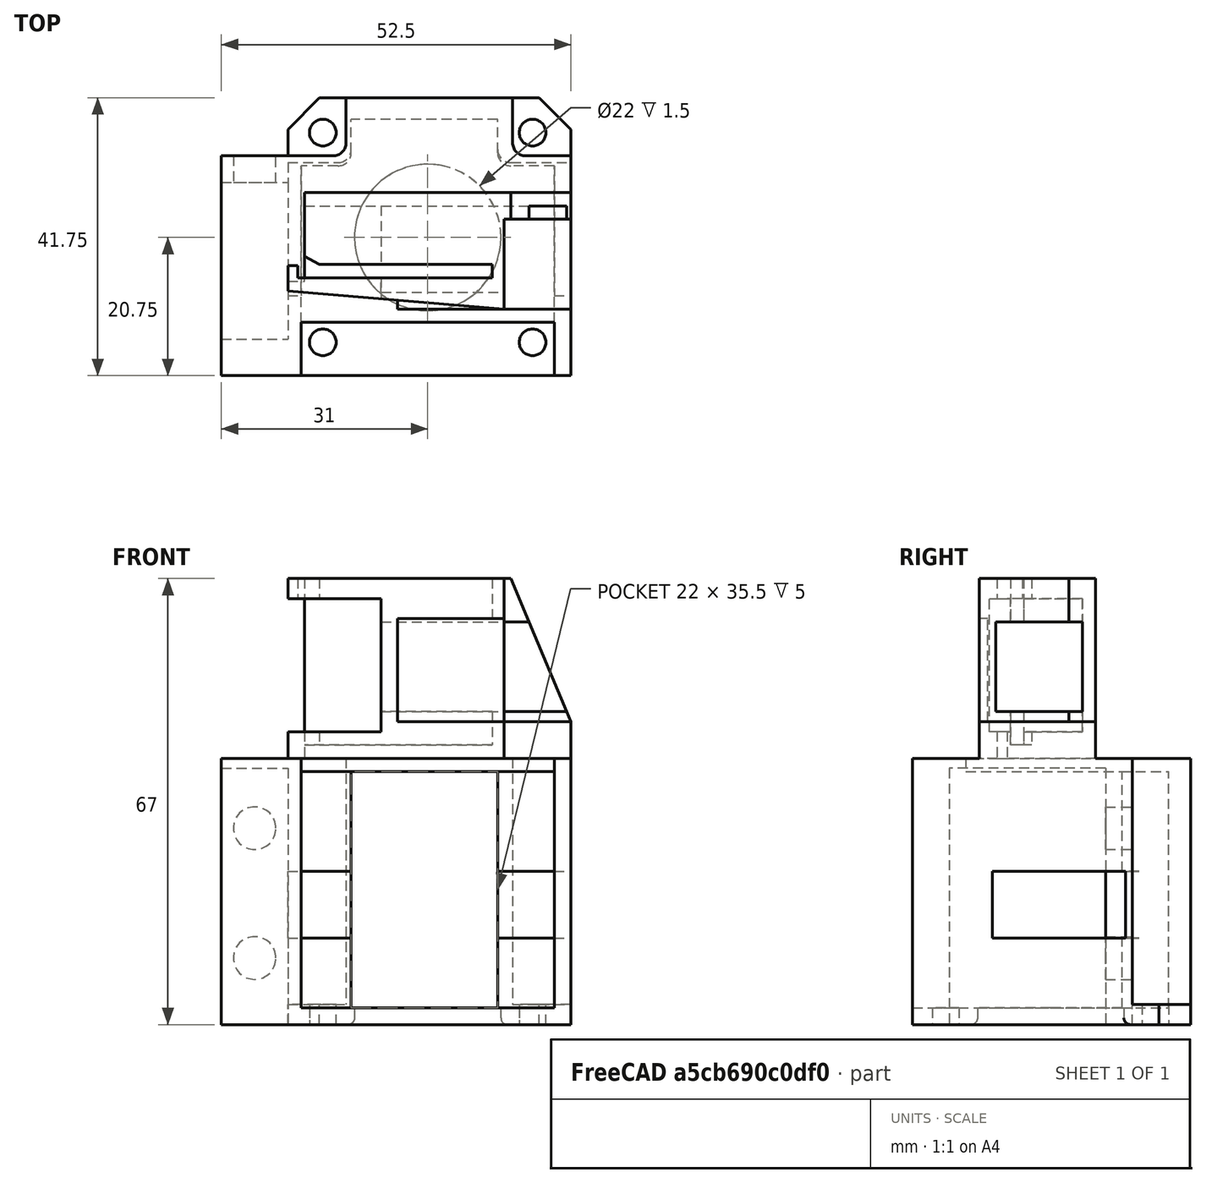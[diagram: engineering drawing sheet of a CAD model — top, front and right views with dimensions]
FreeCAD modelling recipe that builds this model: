
FCSTD DOCUMENT  (FreeCAD 0.20R29410 (Git))
Label: drive_holder
License: All rights reserved
LicenseURL: http://en.wikipedia.org/wiki/All_rights_reserved
objects: Sketcher::SketchObject×20, PartDesign::Pocket×17, PartDesign::Pad×3, PartDesign::Fillet×3, PartDesign::Body×2, Part::Fuse×1, Mesh::Feature×1
note: 69 computed .brp shape members not serialized (recipe doc carries the construction recipe); baked Part::Feature solids carry a one-line shape summary decoded from their .brp

FEATURE [Sketcher::SketchObject] Sketch
  FullyConstrained = true
  MapMode = 5
  Support = -> [XY_Plane]
  sketch-geometry (8):
    g0: LineSegment StartX=0 StartY=0 StartZ=0 EndX=-52.5 EndY=0 EndZ=0
    g1: LineSegment StartX=-52.5 StartY=0 StartZ=0 EndX=-52.5 EndY=33 EndZ=0
    g2: LineSegment StartX=-52.5 StartY=33 StartZ=0 EndX=-42.5 EndY=33 EndZ=0
    g3: LineSegment StartX=-42.5 StartY=33 StartZ=0 EndX=-42.5 EndY=37 EndZ=0
    g4: LineSegment StartX=-42.5 StartY=37 StartZ=0 EndX=-37.75 EndY=41.75 EndZ=0
    g5: LineSegment StartX=-37.75 StartY=41.75 StartZ=0 EndX=-4.75 EndY=41.75 EndZ=0
    g6: LineSegment StartX=-4.75 StartY=41.75 StartZ=0 EndX=0 EndY=37 EndZ=0
    g7: LineSegment StartX=0 StartY=37 StartZ=0 EndX=0 EndY=0 EndZ=0
  constraints (23):
    c: Coincident(g0,g-1)
    c: PointOnObject(g0,g-1)
    c: Coincident(g1,g0)
    c: Vertical(g1)
    c: Coincident(g2,g1)
    c: Horizontal(g2)
    c: Coincident(g3,g2)
    c: Vertical(g3)
    c: Coincident(g4,g3)
    c: Coincident(g5,g4)
    c: Horizontal(g5)
    c: Coincident(g6,g5)
    c: PointOnObject(g6,g-2)
    c: Coincident(g7,g6)
    c: Coincident(g7,g0)
    c: DistanceX(g5,g5) = 33
    c: DistanceX(g0,g0) = 52.5
    c: DistanceX(g2,g2) = 10
    c: Horizontal(g3,g6)
    c: Angle(g5,g6) = 2.35619
    c: Angle(g4,g5) = 2.35619
    c: DistanceY(g0,g6) = 37
    c: DistanceY(g1,g1) = 33
FEATURE [PartDesign::Pad] Pad  label="to_drive_bodie"
  Direction = (0,0,1)
  Length = 40
  Length2 = 10
  Profile = -> Sketch
  ReferenceAxis = -> Sketch [N_Axis]
  Type = 0
FEATURE [Sketcher::SketchObject] Sketch001
  ExternalGeometry = -> [Pad]
  FullyConstrained = true
  MapMode = 5
  Placement = pos=(0,0,40) rot=(0,0,1;0rad)
  Support = -> [Pad]
  sketch-geometry (10):
    g0: LineSegment StartX=-42.5 StartY=33 StartZ=0 EndX=-42.5 EndY=37 EndZ=0
    g1: LineSegment StartX=-42.5 StartY=37 StartZ=0 EndX=-37.75 EndY=41.75 EndZ=0
    g2: LineSegment StartX=-37.75 StartY=41.75 StartZ=0 EndX=-33.75 EndY=41.75 EndZ=0
    g3: LineSegment StartX=-33.75 StartY=41.75 StartZ=0 EndX=-33.75 EndY=33 EndZ=0
    g4: LineSegment StartX=-33.75 StartY=33 StartZ=0 EndX=-42.5 EndY=33 EndZ=0
    g5: LineSegment StartX=-8.75 StartY=41.75 StartZ=0 EndX=-4.75 EndY=41.75 EndZ=0
    g6: LineSegment StartX=-4.75 StartY=41.75 StartZ=0 EndX=0 EndY=37 EndZ=0
    g7: LineSegment StartX=0 StartY=37 StartZ=0 EndX=0 EndY=33 EndZ=0
    g8: LineSegment StartX=0 StartY=33 StartZ=0 EndX=-8.75 EndY=33 EndZ=0
    g9: LineSegment StartX=-8.75 StartY=33 StartZ=0 EndX=-8.75 EndY=41.75 EndZ=0
  constraints (26):
    c: Coincident(g1,g0)
    c: Coincident(g2,g1)
    c: Coincident(g3,g2)
    c: Vertical(g3)
    c: Coincident(g4,g3)
    c: Coincident(g4,g0)
    c: Horizontal(g4)
    c: Coincident(g6,g5)
    c: Coincident(g7,g6)
    c: Coincident(g8,g7)
    c: Horizontal(g8)
    c: Coincident(g9,g8)
    c: Coincident(g9,g5)
    c: Vertical(g9)
    c: Vertical(g7)
    c: Horizontal(g2)
    c: Horizontal(g5)
    c: Coincident(g5,g-3)
    c: Coincident(g6,g-3)
    c: Coincident(g-4,g1)
    c: Coincident(g0,g-4)
    c: Equal(g0,g2)
    c: Equal(g2,g5)
    c: Equal(g5,g7)
    c: Coincident(g0,g-5)
    c: DistanceX(g2,g2) = 4
FEATURE [PartDesign::Pocket] Pocket  label="to_drive_screw_handler"
  BaseFeature = -> Pad
  Direction = (0,0,-1)
  Length = 37
  Length2 = 5
  Profile = -> Sketch001
  ReferenceAxis = -> Sketch001 [N_Axis]
  Type = 0
FEATURE [Sketcher::SketchObject] Sketch002
  ExternalGeometry = -> [Pocket]
  FullyConstrained = true
  MapMode = 5
  Placement = pos=(0,0,0) rot=(1,0,0;3.14159rad)
  Support = -> [Pocket]
  sketch-geometry (2):
    g0: Circle CenterX=-37.25 CenterY=-36.5 CenterZ=0 NormalX=0 NormalY=0 NormalZ=1 AngleXU=0 Radius=2
    g1: Circle CenterX=-5.75 CenterY=-36.5 CenterZ=0 NormalX=0 NormalY=0 NormalZ=1 AngleXU=0 Radius=2
  constraints (6):
    c: DistanceX(g0,g1) = 31.5
    c: Equal(g0,g1)
    c: Diameter(g0) = 4
    c: Horizontal(g1,g0)
    c: DistanceX(g-4,g0) = 0.5
    c: DistanceY(g-3,g0) = 0.5
FEATURE [PartDesign::Pocket] Pocket001  label="to_drive_screw_hole_upper"
  BaseFeature = -> Pocket
  Direction = (0,0,1)
  Length = 3
  Length2 = 5
  Profile = -> Sketch002
  ReferenceAxis = -> Sketch002 [N_Axis]
  Type = 0
FEATURE [Sketcher::SketchObject] Sketch003
  ExternalGeometry = -> [Pocket001]
  FullyConstrained = true
  MapMode = 5
  Placement = pos=(0,0,0) rot=(1,0,0;3.14159rad)
  Support = -> [Pocket001]
  sketch-geometry (2):
    g0: Circle CenterX=-37.25 CenterY=-5 CenterZ=0 NormalX=0 NormalY=0 NormalZ=1 AngleXU=0 Radius=2
    g1: Circle CenterX=-5.75 CenterY=-5 CenterZ=0 NormalX=0 NormalY=0 NormalZ=1 AngleXU=0 Radius=2
  constraints (6):
    c: Equal(g1,g0)
    c: Vertical(g1,g-4)
    c: Vertical(g0,g-3)
    c: Horizontal(g0,g1)
    c: Equal(g1,g-4)
    c: DistanceY(g-3,g0) = 31.5
FEATURE [PartDesign::Pocket] Pocket002  label="to_drive_screw_hole_lower"
  BaseFeature = -> Pocket001
  Direction = (0,0,1)
  Length = 3
  Length2 = 5
  Profile = -> Sketch003
  ReferenceAxis = -> Sketch003 [N_Axis]
  Type = 0
FEATURE [Sketcher::SketchObject] Sketch004
  ExternalGeometry = -> [Pocket002]
  FullyConstrained = true
  MapMode = 5
  Placement = pos=(0,0,0) rot=(1,0,0;3.14159rad)
  Support = -> [Pocket002]
  sketch-geometry (3):
    g0: LineSegment StartX=-37.25 StartY=-5 StartZ=0 EndX=-5.75 EndY=-36.5 EndZ=0
    g1: LineSegment StartX=-5.75 StartY=-5 StartZ=0 EndX=-37.25 EndY=-36.5 EndZ=0
    g2: Circle CenterX=-21.5 CenterY=-20.75 CenterZ=0 NormalX=0 NormalY=0 NormalZ=1 AngleXU=0 Radius=11
  constraints (7):
    c: Coincident(g0,g-3)
    c: Coincident(g0,g-5)
    c: Coincident(g1,g-4)
    c: Coincident(g1,g-6)
    c: PointOnObject(g2,g0)
    c: PointOnObject(g2,g1)
    c: Diameter(g2) = 22
FEATURE [PartDesign::Pocket] Pocket003  label="to_drive_hole"
  BaseFeature = -> Pocket002
  Direction = (0,0,1)
  Length = 5
  Length2 = 5
  Profile = -> Sketch004
  ReferenceAxis = -> Sketch004 [N_Axis]
  Type = 0
FEATURE [Sketcher::SketchObject] Sketch005
  ExternalGeometry = -> [Pocket003]
  FullyConstrained = true
  MapMode = 5
  Placement = pos=(-52.5,0,0) rot=(0.57735,-0.57735,-0.57735;2.0944rad)
  Support = -> [Pocket003]
  sketch-geometry (4):
    g0: LineSegment StartX=-29 StartY=38.5 StartZ=0 EndX=-5.5 EndY=38.5 EndZ=0
    g1: LineSegment StartX=-5.5 StartY=38.5 StartZ=0 EndX=-5.5 EndY=0 EndZ=0
    g2: LineSegment StartX=-29 StartY=0 StartZ=0 EndX=-5.5 EndY=0 EndZ=0
    g3: LineSegment StartX=-29 StartY=38.5 StartZ=0 EndX=-29 EndY=0 EndZ=0
  constraints (12):
    c: DistanceX(g-3,g2) = 4
    c: DistanceY(g0,g-5) = 1.5
    c: Horizontal(g0)
    c: DistanceX(g0,g-5) = 5.5
    c: Coincident(g1,g0)
    c: Vertical(g1)
    c: PointOnObject(g1,g-3)
    c: Coincident(g2,g1)
    c: Coincident(g3,g0)
    c: Vertical(g3)
    c: Coincident(g2,g3)
    c: PointOnObject(g2,g-3)
FEATURE [PartDesign::Pocket] Pocket004  label="to_guide_holder"
  BaseFeature = -> Pocket003
  Direction = (1,0,0)
  Length = 10
  Length2 = 5
  Profile = -> Sketch005
  ReferenceAxis = -> Sketch005 [N_Axis]
  Type = 0
FEATURE [Sketcher::SketchObject] Sketch006
  FullyConstrained = true
  MapMode = 5
  Placement = pos=(-42.5,0,0) rot=(0.57735,-0.57735,-0.57735;2.0944rad)
  Support = -> [Pocket004]
  sketch-geometry (8):
    g0: LineSegment StartX=0 StartY=0 StartZ=0 EndX=-32 EndY=0 EndZ=0
    g1: LineSegment StartX=-32 StartY=0 StartZ=0 EndX=-32 EndY=13 EndZ=0
    g2: LineSegment StartX=-32 StartY=13 StartZ=0 EndX=0 EndY=13 EndZ=0
    g3: LineSegment StartX=0 StartY=13 StartZ=0 EndX=0 EndY=0 EndZ=0
    g4: LineSegment StartX=-32 StartY=13 StartZ=0 EndX=-12 EndY=13 EndZ=0
    g5: LineSegment StartX=-12 StartY=13 StartZ=0 EndX=-12 EndY=23 EndZ=0
    g6: LineSegment StartX=-12 StartY=23 StartZ=0 EndX=-32 EndY=23 EndZ=0
    g7: LineSegment StartX=-32 StartY=23 StartZ=0 EndX=-32 EndY=13 EndZ=0
  constraints (22):
    c: Coincident(g0,g1)
    c: Coincident(g1,g2)
    c: Coincident(g2,g3)
    c: Coincident(g3,g0)
    c: Horizontal(g0)
    c: Horizontal(g2)
    c: Vertical(g1)
    c: Vertical(g3)
    c: Coincident(g0,g-1)
    c: Coincident(g4,g5)
    c: Coincident(g5,g6)
    c: Coincident(g6,g7)
    c: Coincident(g7,g4)
    c: Horizontal(g4)
    c: Horizontal(g6)
    c: Vertical(g5)
    c: Vertical(g7)
    c: Coincident(g4,g1)
    c: DistanceY(g3,g3) = 13
    c: DistanceX(g0,g0) = 32
    c: DistanceY(g5,g5) = 10
    c: DistanceX(g6,g6) = 20
FEATURE [PartDesign::Pocket] Pocket005  label="belt_hole"
  BaseFeature = -> Pocket004
  Direction = (1,0,0)
  Length = 5
  Length2 = 5
  Profile = -> Sketch006
  ReferenceAxis = -> Sketch006 [N_Axis]
  Type = 1
FEATURE [Sketcher::SketchObject] Sketch007
  FullyConstrained = true
  MapMode = 5
  Placement = pos=(0,33,0) rot=(0,0.707107,0.707107;3.14159rad)
  Support = -> [Pocket005]
  sketch-geometry (6):
    g0: Circle CenterX=47.5 CenterY=29.5 CenterZ=0 NormalX=0 NormalY=0 NormalZ=1 AngleXU=0 Radius=3.2
    g1: Circle CenterX=47.5 CenterY=10 CenterZ=0 NormalX=0 NormalY=0 NormalZ=1 AngleXU=0 Radius=3.2
    g2: LineSegment StartX=0 StartY=0 StartZ=0 EndX=47.5 EndY=0 EndZ=0
    g3: LineSegment StartX=47.5 StartY=0 StartZ=0 EndX=47.5 EndY=10 EndZ=0
    g4: LineSegment StartX=47.5 StartY=10 StartZ=0 EndX=0 EndY=10 EndZ=0
    g5: LineSegment StartX=0 StartY=10 StartZ=0 EndX=0 EndY=0 EndZ=0
  constraints (16):
    c: Equal(g0,g1)
    c: Radius(g0) = 3.2
    c: Coincident(g2,g3)
    c: Coincident(g3,g4)
    c: Coincident(g4,g5)
    c: Coincident(g5,g2)
    c: Horizontal(g2)
    c: Horizontal(g4)
    c: Vertical(g3)
    c: Vertical(g5)
    c: Coincident(g3,g1)
    c: DistanceY(g3,g3) = 10
    c: DistanceY(g1,g0) = 19.5
    c: Coincident(g-1,g2)
    c: Vertical(g1,g0)
    c: DistanceX(g2,g2) = 47.5
FEATURE [PartDesign::Pocket] Pocket006  label="to_guide_screw_hole"
  BaseFeature = -> Pocket005
  Direction = (0,-1,2e-16)
  Length = 4
  Length2 = 5
  Profile = -> Sketch007
  ReferenceAxis = -> Sketch007 [N_Axis]
  Type = 0
FEATURE [Sketcher::SketchObject] Sketch008
  FullyConstrained = true
  MapMode = 5
  Placement = pos=(0,0,40) rot=(0,0,1;0rad)
  Support = -> [Pocket006]
  sketch-geometry (4):
    g0: LineSegment StartX=-2.5 StartY=0 StartZ=0 EndX=-40.5 EndY=0 EndZ=0
    g1: LineSegment StartX=-40.5 StartY=0 StartZ=0 EndX=-40.5 EndY=8 EndZ=0
    g2: LineSegment StartX=-40.5 StartY=8 StartZ=0 EndX=-2.5 EndY=8 EndZ=0
    g3: LineSegment StartX=-2.5 StartY=8 StartZ=0 EndX=-2.5 EndY=0 EndZ=0
  constraints (12):
    c: Coincident(g0,g1)
    c: Coincident(g1,g2)
    c: Coincident(g2,g3)
    c: Coincident(g3,g0)
    c: Horizontal(g0)
    c: Horizontal(g2)
    c: Vertical(g1)
    c: Vertical(g3)
    c: PointOnObject(g0,g-1)
    c: DistanceX(g2,g2) = 38
    c: DistanceY(g1,g1) = 8
    c: DistanceX(g0,g-1) = 2.5
FEATURE [PartDesign::Pocket] Pocket007  label="to_drive_inner_hole1"
  BaseFeature = -> Pocket006
  Direction = (0,0,-1)
  Length = 2
  Length2 = 5
  Profile = -> Sketch008
  ReferenceAxis = -> Sketch008 [N_Axis]
  Type = 0
FEATURE [Sketcher::SketchObject] Sketch009
  FullyConstrained = true
  MapMode = 5
  Placement = pos=(0,0,0) rot=(1,0,0;1.5708rad)
  Support = -> [Pocket007]
  sketch-geometry (8):
    g0: LineSegment StartX=-2.5 StartY=2.5 StartZ=0 EndX=-40.5 EndY=2.5 EndZ=0
    g1: LineSegment StartX=-40.5 StartY=2.5 StartZ=0 EndX=-40.5 EndY=38 EndZ=0
    g2: LineSegment StartX=-40.5 StartY=38 StartZ=0 EndX=-2.5 EndY=38 EndZ=0
    g3: LineSegment StartX=-2.5 StartY=38 StartZ=0 EndX=-2.5 EndY=2.5 EndZ=0
    g4: LineSegment StartX=0 StartY=0 StartZ=0 EndX=-2.5 EndY=0 EndZ=0
    g5: LineSegment StartX=-2.5 StartY=0 StartZ=0 EndX=-2.5 EndY=2.5 EndZ=0
    g6: LineSegment StartX=-2.5 StartY=2.5 StartZ=0 EndX=0 EndY=2.5 EndZ=0
    g7: LineSegment StartX=0 StartY=2.5 StartZ=0 EndX=0 EndY=0 EndZ=0
  constraints (22):
    c: Coincident(g0,g1)
    c: Coincident(g1,g2)
    c: Coincident(g2,g3)
    c: Coincident(g3,g0)
    c: Horizontal(g0)
    c: Horizontal(g2)
    c: Vertical(g1)
    c: Vertical(g3)
    c: Coincident(g4,g5)
    c: Coincident(g5,g6)
    c: Coincident(g6,g7)
    c: Coincident(g7,g4)
    c: Horizontal(g4)
    c: Horizontal(g6)
    c: Vertical(g5)
    c: Vertical(g7)
    c: Coincident(g4,g-1)
    c: Coincident(g5,g0)
    c: DistanceY(g7,g7) = 2.5
    c: DistanceX(g6,g6) = 2.5
    c: DistanceY(g3,g3) = 35.5
    c: DistanceX(g2,g2) = 38
FEATURE [PartDesign::Pocket] Pocket008  label="to_drive_inner_hole2"
  BaseFeature = -> Pocket007
  Direction = (0,1,-2e-16)
  Length = 31.5
  Length2 = 5
  Profile = -> Sketch009
  ReferenceAxis = -> Sketch009 [N_Axis]
  Type = 0
FEATURE [Sketcher::SketchObject] Sketch010
  FullyConstrained = true
  MapMode = 5
  Placement = pos=(0,31.5,-6.9e-15) rot=(1,0,0;1.5708rad)
  Support = -> [Pocket008]
  sketch-geometry (8):
    g0: LineSegment StartX=-33 StartY=38 StartZ=0 EndX=-11 EndY=38 EndZ=0
    g1: LineSegment StartX=-11 StartY=38 StartZ=0 EndX=-11 EndY=2.5 EndZ=0
    g2: LineSegment StartX=-11 StartY=2.5 StartZ=0 EndX=-33 EndY=2.5 EndZ=0
    g3: LineSegment StartX=-33 StartY=2.5 StartZ=0 EndX=-33 EndY=38 EndZ=0
    g4: LineSegment StartX=0 StartY=0 StartZ=0 EndX=-11 EndY=0 EndZ=0
    g5: LineSegment StartX=-11 StartY=0 StartZ=0 EndX=-11 EndY=2.5 EndZ=0
    g6: LineSegment StartX=-11 StartY=2.5 StartZ=0 EndX=0 EndY=2.5 EndZ=0
    g7: LineSegment StartX=0 StartY=2.5 StartZ=0 EndX=0 EndY=0 EndZ=0
  constraints (22):
    c: Coincident(g0,g1)
    c: Coincident(g1,g2)
    c: Coincident(g2,g3)
    c: Coincident(g3,g0)
    c: Horizontal(g0)
    c: Horizontal(g2)
    c: Vertical(g1)
    c: Vertical(g3)
    c: DistanceX(g0,g0) = 22
    c: Coincident(g4,g5)
    c: Coincident(g5,g6)
    c: Coincident(g6,g7)
    c: Coincident(g7,g4)
    c: Horizontal(g4)
    c: Horizontal(g6)
    c: Vertical(g5)
    c: Vertical(g7)
    c: Coincident(g5,g1)
    c: DistanceX(g6,g6) = 11
    c: DistanceY(g5,g5) = 2.5
    c: Coincident(g4,g-1)
    c: DistanceY(g1,g1) = 35.5
FEATURE [PartDesign::Pocket] Pocket009  label="to_drive_inner_hole3"
  BaseFeature = -> Pocket008
  Direction = (0,1,-2e-16)
  Length = 7
  Length2 = 5
  Profile = -> Sketch010
  ReferenceAxis = -> Sketch010 [N_Axis]
  Type = 0
FEATURE [Sketcher::SketchObject] Sketch011
  FullyConstrained = true
  MapMode = 5
  Support = -> [XY_Plane001]
  sketch-geometry (4):
    g0: LineSegment StartX=-42.5 StartY=27.5 StartZ=0 EndX=0 EndY=27.5 EndZ=0
    g1: LineSegment StartX=0 StartY=27.5 StartZ=0 EndX=0 EndY=10 EndZ=0
    g2: LineSegment StartX=0 StartY=10 StartZ=0 EndX=-42.5 EndY=10 EndZ=0
    g3: LineSegment StartX=-42.5 StartY=10 StartZ=0 EndX=-42.5 EndY=27.5 EndZ=0
  constraints (12):
    c: Coincident(g0,g1)
    c: Coincident(g1,g2)
    c: Coincident(g2,g3)
    c: Coincident(g3,g0)
    c: Horizontal(g0)
    c: Horizontal(g2)
    c: Vertical(g1)
    c: Vertical(g3)
    c: PointOnObject(g1,g-2)
    c: DistanceY(g-1,g1) = 10
    c: DistanceY(g1,g1) = 17.5
    c: DistanceX(g0,g0) = 42.5
FEATURE [PartDesign::Pad] Pad001  label="body"
  Direction = (0,0,1)
  Length = 27
  Length2 = 10
  Profile = -> Sketch011
  ReferenceAxis = -> Sketch011 [N_Axis]
  Type = 0
FEATURE [Sketcher::SketchObject] Sketch012
  ExternalGeometry = -> [Pad001]
  FullyConstrained = true
  MapMode = 5
  Placement = pos=(0,27.5,0) rot=(0,0.707107,0.707107;3.14159rad)
  Support = -> [Pad001]
  sketch-geometry (3):
    g0: LineSegment StartX=0 StartY=27 StartZ=0 EndX=9 EndY=27 EndZ=0
    g1: LineSegment StartX=9 StartY=27 StartZ=0 EndX=0 EndY=5.5 EndZ=0
    g2: LineSegment StartX=0 StartY=5.5 StartZ=0 EndX=0 EndY=27 EndZ=0
  constraints (8):
    c: Coincident(g0,g-4)
    c: PointOnObject(g0,g-4)
    c: Coincident(g1,g0)
    c: PointOnObject(g1,g-3)
    c: Coincident(g2,g1)
    c: Coincident(g2,g0)
    c: DistanceX(g0,g0) = 9
    c: DistanceY(g2,g2) = 21.5
FEATURE [PartDesign::Pocket] Pocket010  label="right_body_champfer"
  BaseFeature = -> Pad001
  Direction = (0,-1,2e-16)
  Length = 6
  Length2 = 5
  Profile = -> Sketch012
  ReferenceAxis = -> Sketch012 [N_Axis]
  Type = 1
FEATURE [Sketcher::SketchObject] Sketch013
  ExternalGeometry = -> [Pocket010]
  FullyConstrained = true
  MapMode = 5
  Placement = pos=(0,0,0) rot=(0.57735,0.57735,0.57735;2.0944rad)
  Support = -> [Pocket010]
  sketch-geometry (4):
    g0: LineSegment StartX=10 StartY=27 StartZ=0 EndX=23.5 EndY=27 EndZ=0
    g1: LineSegment StartX=23.5 StartY=27 StartZ=0 EndX=23.5 EndY=5.5 EndZ=0
    g2: LineSegment StartX=23.5 StartY=5.5 StartZ=0 EndX=10 EndY=5.5 EndZ=0
    g3: LineSegment StartX=10 StartY=5.5 StartZ=0 EndX=10 EndY=27 EndZ=0
  constraints (11):
    c: Coincident(g0,g1)
    c: Coincident(g1,g2)
    c: Coincident(g2,g3)
    c: Coincident(g3,g0)
    c: Horizontal(g0)
    c: Horizontal(g2)
    c: Vertical(g1)
    c: Vertical(g3)
    c: Coincident(g0,g-4)
    c: PointOnObject(g1,g-3)
    c: DistanceX(g1,g-3) = 4
FEATURE [PartDesign::Pocket] Pocket011  label="right_body_champfer_hole"
  BaseFeature = -> Pocket010
  Direction = (-1,0,0)
  Length = 10
  Length2 = 5
  Profile = -> Sketch013
  ReferenceAxis = -> Sketch013 [N_Axis]
  Type = 0
FEATURE [Sketcher::SketchObject] Sketch014
  ExternalGeometry = -> [Pocket011]
  FullyConstrained = true
  MapMode = 5
  Placement = pos=(0,0,27) rot=(0,0,1;0rad)
  Support = -> [Pocket011]
  sketch-geometry (3):
    g0: LineSegment StartX=-42.5 StartY=12.7 StartZ=0 EndX=-42.5 EndY=10 EndZ=0
    g1: LineSegment StartX=-42.5 StartY=12.7 StartZ=0 EndX=-10 EndY=10 EndZ=0
    g2: LineSegment StartX=-10 StartY=10 StartZ=0 EndX=-42.5 EndY=10 EndZ=0
  constraints (7):
    c: PointOnObject(g0,g-4)
    c: Coincident(g0,g-4)
    c: Coincident(g1,g0)
    c: Coincident(g1,g-3)
    c: Coincident(g2,g1)
    c: Coincident(g2,g0)
    c: DistanceY(g0,g0) = 2.7
FEATURE [PartDesign::Pocket] Pocket012  label="bottom_pcb_anker_champfer"
  BaseFeature = -> Pocket011
  Direction = (0,0,-1)
  Length = 27
  Length2 = 5
  Profile = -> Sketch014
  ReferenceAxis = -> Sketch014 [N_Axis]
  Type = 0
FEATURE [Sketcher::SketchObject] Sketch015
  ExternalGeometry = -> [Pocket012]
  FullyConstrained = true
  MapMode = 5
  Placement = pos=(-42.5,0,0) rot=(0.57735,-0.57735,-0.57735;2.0944rad)
  Support = -> [Pocket012]
  sketch-geometry (6):
    g0: LineSegment StartX=-27.5 StartY=27 StartZ=0 EndX=-16.5 EndY=27 EndZ=0
    g1: LineSegment StartX=-27.5 StartY=0 StartZ=0 EndX=-27.5 EndY=27 EndZ=0
    g2: LineSegment StartX=-27.5 StartY=0 StartZ=0 EndX=-14.2 EndY=0 EndZ=0
    g3: LineSegment StartX=-16.5 StartY=27 StartZ=0 EndX=-16.5 EndY=24 EndZ=0
    g4: LineSegment StartX=-16.5 StartY=24 StartZ=0 EndX=-14.2 EndY=24 EndZ=0
    g5: LineSegment StartX=-14.2 StartY=24 StartZ=0 EndX=-14.2 EndY=0 EndZ=0
  constraints (17):
    c: Horizontal(g0)
    c: Vertical(g1)
    c: DistanceX(g0,g0) = 11
    c: Coincident(g2,g1)
    c: Coincident(g3,g0)
    c: Vertical(g3)
    c: Coincident(g4,g3)
    c: Horizontal(g4)
    c: Coincident(g5,g4)
    c: Coincident(g5,g2)
    c: Vertical(g5)
    c: DistanceY(g3,g3) = 3
    c: DistanceX(g2,g-4) = 1.5
    c: Coincident(g1,g0)
    c: Horizontal(g2)
    c: PointOnObject(g2,g-1)
    c: Coincident(g0,g-5)
FEATURE [PartDesign::Pocket] Pocket016  label="left_side_hole"
  BaseFeature = -> Pocket012
  Direction = (1,0,0)
  Length = 2.5
  Length2 = 5
  Profile = -> Sketch015
  ReferenceAxis = -> Sketch015 [N_Axis]
  Type = 0
FEATURE [Sketcher::SketchObject] Sketch016
  ExternalGeometry = -> [Pocket016]
  FullyConstrained = true
  MapMode = 5
  Placement = pos=(-42.5,0,0) rot=(0.57735,-0.57735,-0.57735;2.0944rad)
  Support = -> [Pocket016]
  sketch-geometry (8):
    g0: LineSegment StartX=-10 StartY=24 StartZ=0 EndX=-25.5 EndY=24 EndZ=0
    g1: LineSegment StartX=-25.5 StartY=24 StartZ=0 EndX=-25.5 EndY=4 EndZ=0
    g2: LineSegment StartX=-25.5 StartY=4 StartZ=0 EndX=-10 EndY=4 EndZ=0
    g3: LineSegment StartX=-10 StartY=4 StartZ=0 EndX=-10 EndY=24 EndZ=0
    g4: LineSegment StartX=-27.5 StartY=27 StartZ=0 EndX=-25.5 EndY=27 EndZ=0
    g5: LineSegment StartX=-25.5 StartY=27 StartZ=0 EndX=-25.5 EndY=24 EndZ=0
    g6: LineSegment StartX=-25.5 StartY=24 StartZ=0 EndX=-27.5 EndY=24 EndZ=0
    g7: LineSegment StartX=-27.5 StartY=24 StartZ=0 EndX=-27.5 EndY=27 EndZ=0
  constraints (22):
    c: Coincident(g0,g1)
    c: Coincident(g1,g2)
    c: Coincident(g2,g3)
    c: Coincident(g3,g0)
    c: Horizontal(g0)
    c: Horizontal(g2)
    c: Vertical(g1)
    c: Vertical(g3)
    c: DistanceY(g1,g1) = 20
    c: Coincident(g4,g5)
    c: Coincident(g5,g6)
    c: Coincident(g6,g7)
    c: Coincident(g7,g4)
    c: Horizontal(g4)
    c: Horizontal(g6)
    c: Vertical(g5)
    c: Vertical(g7)
    c: Coincident(g4,g-3)
    c: Coincident(g5,g0)
    c: DistanceX(g4,g4) = 2
    c: DistanceY(g7,g7) = 3
    c: PointOnObject(g0,g-4)
FEATURE [PartDesign::Pocket] Pocket017  label="pcb_inner_hole1"
  BaseFeature = -> Pocket016
  Direction = (1,0,0)
  Length = 14
  Length2 = 5
  Profile = -> Sketch016
  ReferenceAxis = -> Sketch016 [N_Axis]
  Type = 0
FEATURE [Sketcher::SketchObject] Sketch017
  ExternalGeometry = -> [Pocket017]
  FullyConstrained = true
  MapMode = 5
  Placement = pos=(-10,0,0) rot=(0.57735,0.57735,0.57735;2.0944rad)
  Support = -> [Pocket017]
  sketch-geometry (4):
    g0: LineSegment StartX=10 StartY=21 StartZ=0 EndX=12 EndY=21 EndZ=0
    g1: LineSegment StartX=12 StartY=21 StartZ=0 EndX=12 EndY=5.5 EndZ=0
    g2: LineSegment StartX=12 StartY=5.5 StartZ=0 EndX=10 EndY=5.5 EndZ=0
    g3: LineSegment StartX=10 StartY=5.5 StartZ=0 EndX=10 EndY=21 EndZ=0
  constraints (12):
    c: Coincident(g0,g1)
    c: Coincident(g1,g2)
    c: Coincident(g2,g3)
    c: Coincident(g3,g0)
    c: Horizontal(g0)
    c: Horizontal(g2)
    c: Vertical(g1)
    c: Vertical(g3)
    c: PointOnObject(g0,g-3)
    c: DistanceY(g0,g-3) = 6
    c: DistanceX(g0,g0) = 2
    c: DistanceY(g-4,g2) = 5.5
FEATURE [PartDesign::Pad] Pad002  label="pcb_bottom_plate"
  BaseFeature = -> Pocket017
  Direction = (1,0,0)
  Length = 16
  Length2 = 10
  Profile = -> Sketch017
  ReferenceAxis = -> Sketch017 [N_Axis]
  Reversed = true
  Type = 0
FEATURE [Sketcher::SketchObject] Sketch018
  ExternalGeometry = -> [Pad002]
  FullyConstrained = true
  MapMode = 5
  Placement = pos=(-28.5,0,0) rot=(0.57735,-0.57735,-0.57735;2.0944rad)
  Support = -> [Pad002]
  sketch-geometry (8):
    g0: LineSegment StartX=-25.5 StartY=20.5 StartZ=0 EndX=-12.5 EndY=20.5 EndZ=0
    g1: LineSegment StartX=-12.5 StartY=20.5 StartZ=0 EndX=-12.5 EndY=7 EndZ=0
    g2: LineSegment StartX=-12.5 StartY=7 StartZ=0 EndX=-25.5 EndY=7 EndZ=0
    g3: LineSegment StartX=-25.5 StartY=7 StartZ=0 EndX=-25.5 EndY=20.5 EndZ=0
    g4: LineSegment StartX=-27.5 StartY=27 StartZ=0 EndX=-25.5 EndY=27 EndZ=0
    g5: LineSegment StartX=-25.5 StartY=27 StartZ=0 EndX=-25.5 EndY=20.5 EndZ=0
    g6: LineSegment StartX=-25.5 StartY=20.5 StartZ=0 EndX=-27.5 EndY=20.5 EndZ=0
    g7: LineSegment StartX=-27.5 StartY=20.5 StartZ=0 EndX=-27.5 EndY=27 EndZ=0
  constraints (22):
    c: Coincident(g0,g1)
    c: Coincident(g1,g2)
    c: Coincident(g2,g3)
    c: Coincident(g3,g0)
    c: Horizontal(g0)
    c: Horizontal(g2)
    c: Vertical(g1)
    c: Vertical(g3)
    c: Coincident(g4,g5)
    c: Coincident(g5,g6)
    c: Coincident(g6,g7)
    c: Coincident(g7,g4)
    c: Horizontal(g4)
    c: Horizontal(g6)
    c: Vertical(g5)
    c: Vertical(g7)
    c: Coincident(g4,g-3)
    c: Coincident(g5,g0)
    c: DistanceX(g4,g4) = 2
    c: DistanceY(g7,g7) = 6.5
    c: DistanceY(g3,g3) = 13.5
    c: DistanceX(g0,g0) = 13
FEATURE [PartDesign::Pocket] Pocket018  label="pcb_inner_hole2"
  BaseFeature = -> Pad002
  Direction = (1,0,0)
  Length = 5
  Length2 = 5
  Profile = -> Sketch018
  ReferenceAxis = -> Sketch018 [N_Axis]
  Type = 1
FEATURE [Sketcher::SketchObject] Sketch019
  ExternalGeometry = -> [Pocket018]
  FullyConstrained = true
  MapMode = 5
  Placement = pos=(0,0,27) rot=(0,0,1;0rad)
  Support = -> [Pocket018]
  sketch-geometry (6):
    g0: LineSegment StartX=-40 StartY=17.9 StartZ=0 EndX=-37.8 EndY=16.7 EndZ=0
    g1: LineSegment StartX=-37.8 StartY=16.7 StartZ=0 EndX=-11.8 EndY=16.7 EndZ=0
    g2: LineSegment StartX=-11.8 StartY=16.7 StartZ=0 EndX=-11.8 EndY=14.7 EndZ=0
    g3: LineSegment StartX=-11.8 StartY=14.7 StartZ=0 EndX=-41 EndY=14.7 EndZ=0
    g4: LineSegment StartX=-41 StartY=14.7 StartZ=0 EndX=-41 EndY=16.5 EndZ=0
    g5: LineSegment StartX=-41 StartY=16.5 StartZ=0 EndX=-40 EndY=17.9 EndZ=0
  constraints (19):
    c: Coincident(g1,g0)
    c: Horizontal(g1)
    c: Coincident(g2,g1)
    c: Vertical(g2)
    c: Coincident(g3,g2)
    c: Horizontal(g3)
    c: Coincident(g4,g3)
    c: Vertical(g4)
    c: Coincident(g5,g0)
    c: DistanceY(g2,g2) = 2
    c: DistanceX(g3,g2) = 29.2
    c: DistanceX(g2,g-4) = 1.8
    c: DistanceX(g1,g1) = 26
    c: PointOnObject(g0,g-5)
    c: DistanceY(g0,g-5) = 9.6
    c: Coincident(g5,g4)
    c: DistanceY(g-4,g2) = 4.7
    c: DistanceX(g-6,g4) = 1.5
    c: PointOnObject(g4,g-6)
FEATURE [PartDesign::Pocket] Pocket019  label="pcb_handler"
  BaseFeature = -> Pocket018
  Direction = (0,0,-1)
  Length = 25
  Length2 = 5
  Profile = -> Sketch019
  ReferenceAxis = -> Sketch019 [N_Axis]
  Type = 0
FEATURE [PartDesign::Body] Body001  label="microswitch_handler"
  Group = -> [Sketch011,Pad001,Sketch012,Pocket010,Sketch013,Pocket011,Sketch014,Pocket012,Sketch015,Pocket016,Sketch016,Pocket017,Sketch017,Pad002,Sketch018,Pocket018,Sketch019,Pocket019]
  Origin = -> Origin001
  Placement = pos=(0,0,40) rot=(0,0,1;0rad)
  Tip = -> Pocket019
FEATURE [PartDesign::Fillet] Fillet
  Base = -> Pocket009 [Edge110,Edge113,Edge144,Edge151]
  BaseFeature = -> Pocket009
  Radius = 2
  SupportTransform = false
  UseAllEdges = false
FEATURE [PartDesign::Fillet] Fillet001
  Base = -> Fillet [Edge160,Edge156,Edge161,Edge144]
  BaseFeature = -> Fillet
  Radius = 2
  SupportTransform = false
  UseAllEdges = false
FEATURE [PartDesign::Fillet] Fillet002
  Base = -> Fillet001 [Edge39]
  BaseFeature = -> Fillet001
  Radius = 1
  SupportTransform = false
  UseAllEdges = false
FEATURE [PartDesign::Body] Body  label="drive_handler"
  Group = -> [Sketch,Pad,Sketch001,Pocket,Sketch002,Pocket001,Sketch003,Pocket002,Sketch004,Pocket003,Sketch005,Pocket004,Sketch006,Pocket005,Sketch007,Pocket006,Sketch008,Pocket007,Sketch009,Pocket008,Sketch010,Pocket009,Fillet,Fillet001,Fillet002]
  Origin = -> Origin
  Tip = -> Fillet002
FEATURE [Part::Fuse] Fusion  label="ender_s1_Y_stepper_shell"
  Base = -> Body
  Tool = -> Body001
FEATURE [Mesh::Feature] Mesh  label="ender_s1_Y_stepper_shell (Meshed)"
